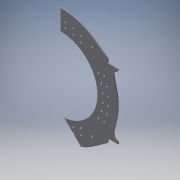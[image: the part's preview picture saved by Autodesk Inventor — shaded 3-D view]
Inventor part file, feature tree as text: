
AUTODESK INVENTOR PART (.ipt)
format: ipt  version: 2016 (Build 200138000, 138)  size: 219,136 bytes
history: native  units: in
note: dims shown in document units (in); Inventor stores cm internally (conversion verified against a paired STEP export)
features: reference x16, extrude x4, sketch x4, projected_geometry x1
ambient origin geometry x8: Origin, YZ Plane, XZ Plane, XY Plane, X Axis, Y Axis, Z Axis, Center Point
bodies: Solid1 (feature_tree)
feature tree (25):
  extrude  "Extrusion1"  Depth=0.125in TaperAngle=0.0deg
  extrude  "Extrusion3"  Depth=0.125in TaperAngle=0.0deg
  extrude  "Extrusion4"  Depth=0.5in
  extrude  "Extrusion5"  Depth=0.125in TaperAngle=0.0deg
  sketch  "Sketch1"  dims[d0=14.0in d1=0.125in d2=0.0in]
  reference  "Reference1"
  reference  "Reference2"
  sketch  "Sketch2"  dims[d3=0.5in d6=0.125in d7=0.0in]
  reference  "Reference3"
  reference  "Reference4"
  reference  "Reference5"
  reference  "Reference6"
  reference  "Reference7"
  reference  "Reference8"
  reference  "Reference9"
  reference  "Reference10"
  reference  "Reference11"
  reference  "Reference12"
  reference  "Reference13"
  reference  "Reference14"
  sketch  "Sketch3"  dims[d8=0.8in d9=0.5in]
  projected_geometry  "Projected Loop1"
  sketch  "Sketch4"  dims[d10=0.125in d11=0.0in d12=0.125in d13=0.0in]
  reference  "Reference15"
  reference  "Reference16"
